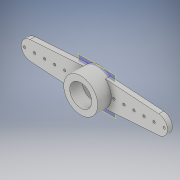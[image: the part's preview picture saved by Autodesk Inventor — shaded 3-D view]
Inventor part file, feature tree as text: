
AUTODESK INVENTOR PART (.ipt)
format: ipt  version: 2017 (Build 210142000, 142)  size: 167,936 bytes
history: native  units: in
note: dims shown in document units (in); Inventor stores cm internally (conversion verified against a paired STEP export)
features: extrude x6, sketch x6, plane x1, pattern_circular x1
ambient origin geometry x8: Origin, YZ Plane, XZ Plane, XY Plane, X Axis, Y Axis, Z Axis, Center Point
bodies: Solid1 (feature_tree)
feature tree (14):
  extrude  "Extrusion1"  Depth=0.159in TaperAngle=0.0deg
  extrude  "Extrusion2"  Depth=0.108in TaperAngle=0.0deg
  extrude  "Extrusion3"  Depth=0.042in TaperAngle=0.0deg
  extrude  "Extrusion4"  Depth=0.042in TaperAngle=0.0deg
  plane  "Work Plane1"
  extrude  "Extrusion5"  Depth=0.16in
  extrude  "Extrusion6"  Depth=0.042in TaperAngle=0.0deg
  pattern_circular  "Circular Pattern1"  [2 undecoded]
  sketch  "Sketch1"  dims[d0=0.291in d1=0.159in d2=0.0in]
  sketch  "Sketch2"  dims[d3=0.051in d4=0.108in d5=0.0in]
  sketch  "Sketch3"  dims[d6=0.06in d7=0.042in d8=0.0in]
  sketch  "Sketch4"  dims[d9=0.114in d10=0.042in d11=0.0in]
  sketch  "Sketch5"  dims[d12=0.222in d13=0.16in]
  sketch  "Sketch6"  dims[d15=0.546in d16=0.042in d17=0.0in d18=0.072in d19=0.158in d20=0.086in d21=0.086in d22=0.086in d23=0.086in d24=0.042in d25=0.0in d26=0.7874in d28=360.0deg d30=0.7874in d31=360.0deg]
note: 2 required parameter values undecoded (feature->parameter linkage not recoverable at this tier; creation-order binding heuristic only, values carry confidence <= 0.55)
